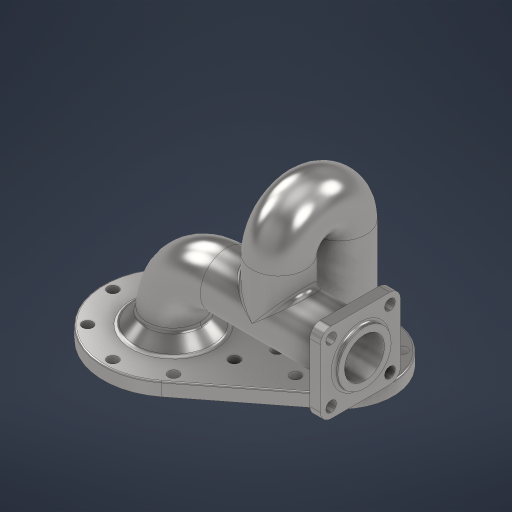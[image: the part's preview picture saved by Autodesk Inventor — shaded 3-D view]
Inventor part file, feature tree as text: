
AUTODESK INVENTOR PART (.ipt)
format: ipt  version: 2023 (Build 270158000, 158)  size: 548,352 bytes
history: native  units: mm
features: sketch x7, extrude x3, fillet x3, revolve x2, sweep x2, plane x2, delete_face x2, projected_geometry x2, other x1
ambient origin geometry x8: Origin, YZ Plane, XZ Plane, XY Plane, X Axis, Y Axis, Z Axis, Center Point
bodies: Solid1 (feature_tree)
feature tree (24):
  sketch  "Sketch1"  dims[d2=30.0deg d4=91.0mm]
  extrude  "Extrusion1"  Depth=91.0mm
  extrude  "Extrusion2"  Depth=40.0mm
  sketch  "Sketch2"  dims[d5=52.5mm d6=40.0mm]
  revolve  "Revolution1"  [1 undecoded]
  revolve  "Revolution2"  [1 undecoded]
  sweep  "Sweep1"
  plane  "Work Plane1"
  extrude  "Extrusion3"  Depth=80.0mm
  plane  "Work Plane2"
  sweep  "Sweep2"
  delete_face  "Delete Face1"
  delete_face  "Delete Face2"
  fillet  "Fillet1"  Radius=10.0mm
  fillet  "Fillet2"  Radius=4.0mm
  fillet  "Fillet3"  Radius=40.0mm
  sketch  "Sketch3"  dims[d8=8.0mm d11=91.0mm]
  sketch  "Sketch4"  dims[d12=66.0mm d13=8.0mm]
  projected_geometry  "Projected Loop1"
  sketch  "Sketch5"  dims[d14=8.0mm d15=80.0mm d17=360.0deg]
  projected_geometry  "Projected Loop2"
  other  "Work Axis1"
  sketch  "Sketch6"  dims[d19=80.0mm d21=360.0deg d26=74.0mm]
  sketch  "Sketch7"  dims[d27=30.0mm d28=30.0mm d29=10.0mm d30=0.0mm d31=4.0mm d32=0.0mm d33=40.0mm d34=20.0mm d35=90.0deg d36=15.0mm d37=90.0deg d38=90.0deg d39=60.0mm d40=143.0mm d41=40.0mm d42=0.0mm d43=0.0mm d44=-3.0mm d45=60.0mm d46=60.0mm d47=8.0mm d48=8.0mm d49=8.0mm d50=0.0mm d51=90.0deg d52=60.0mm d55=22.75mm d56=95.0mm d57=40.0mm d58=0.0mm d59=0.0mm d60=4.0mm d61=1.0mm d62=2.0mm d63=0.0mm d64=0.0mm]
note: 2 required parameter values undecoded (feature->parameter linkage not recoverable at this tier; creation-order binding heuristic only, values carry confidence <= 0.55)
